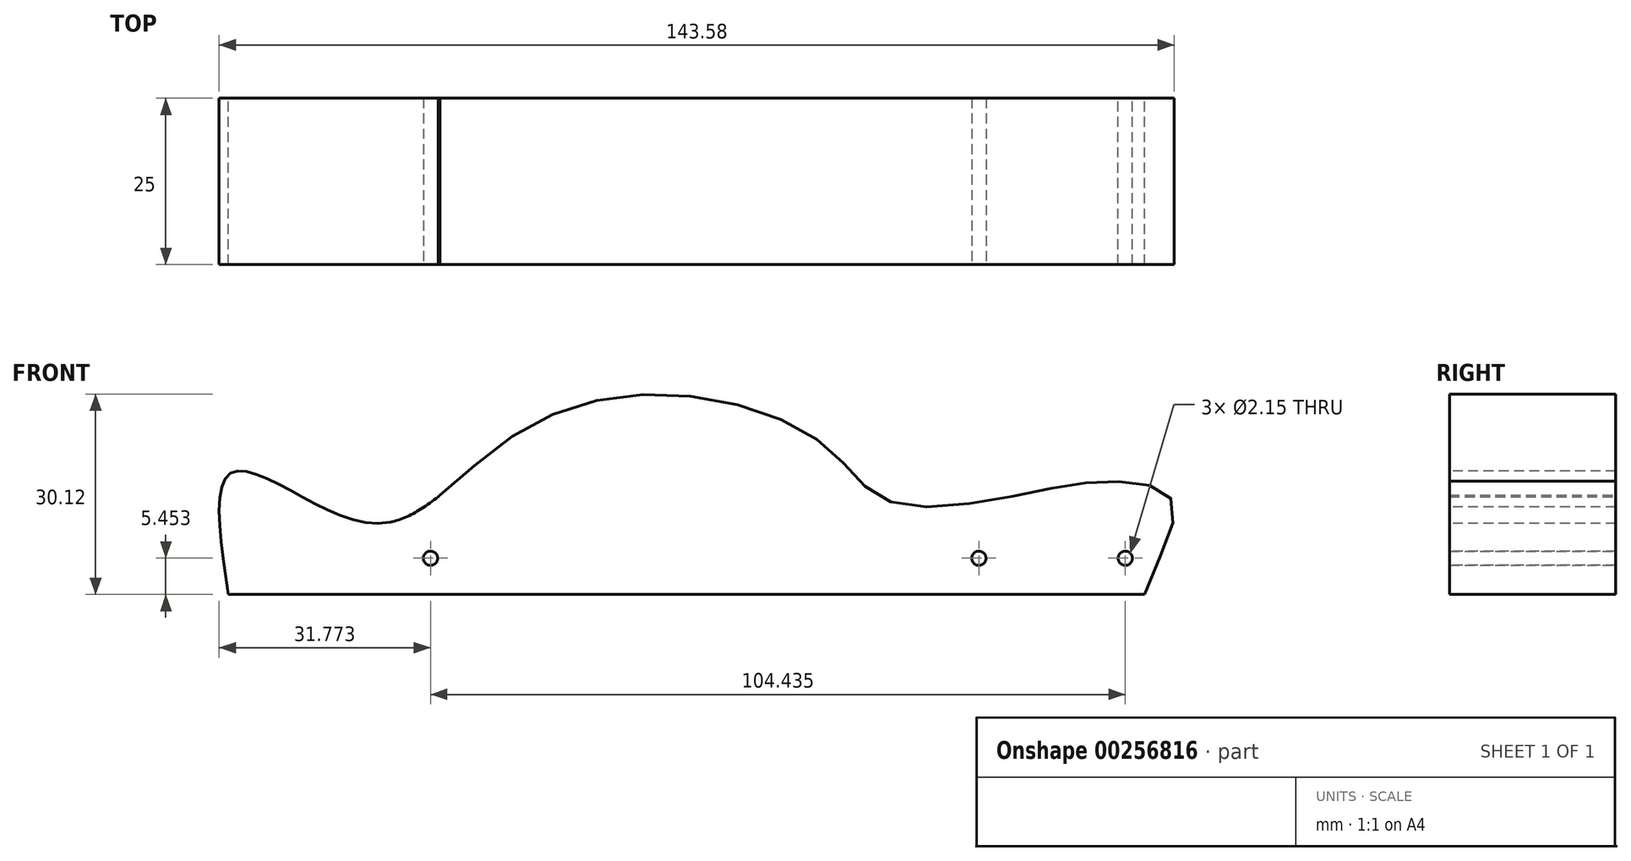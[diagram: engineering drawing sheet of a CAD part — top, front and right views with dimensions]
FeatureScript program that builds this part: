
annotation { "Feature Type Name" : "Feature", "Feature Type Description" : "" }
export const myFeature = defineFeature(function(context is Context, id is Id, definition is map)
    precondition{}
    {
        {
            var Q0;
            Q0=qCreatedBy(makeId("Front.planeOp"),FACE);
            var sketch = newSketch(context, id + "F0", { "sketchPlane" : qUnion([Q0])});
            skLineSegment(sketch, "E0", {"start": v(0, 0) * mm, "end": v(70.1, 0) * mm});
            skLineSegment(sketch, "E1", {"start": v(70.1, 0) * mm, "end": v(-67.63, 0) * mm});
            skFitSpline(sketch, "E2", {"points": [v(-67.63, 0) * mm, v(-67.63, 18) * mm, v(-58.54, 15.78) * mm, v(-43.29, 10.87) * mm, v(-24.86, 23.85) * mm, v(0, 30) * mm, v(22.28, 22.2) * mm, v(31.43, 14.07) * mm, v(51.3, 15) * mm, v(66.46, 17) * mm, v(74.34, 13.86) * mm, v(70.1, 0) * mm, v(67.74, -19.06) * mm], "startDerivative": vector(-41.87, 267.1) * mm, "endDerivative": vector(-3.35, -215.2) * mm});
            skFitSpline(sketch, "E3", {"points": [v(-35.86, 14.9) * mm, v(-36.11, 14.7) * mm, v(-43.29, 10.87) * mm], "startDerivative": vector(2.2, 1.82) * mm, "endDerivative": vector(-12.31, -7.66) * mm});
            skSolve(sketch);
        }
        {
            var Q0;
            {var subQ0=sQuery(id+"F0.wireOp",EDGE,"E2");var subQ1=sQuery(id+"F0.wireOp",EDGE,"E1");var subQ2=makeQuery(id+"F0.imprint","INTERSECT",VERTEX,{"disambiguationData":[OD(0.0)],"derivedFrom":[subQ1,subQ0]});Q0=makeQuery(id+"F0.imprint","IMPRINT",FACE,{"disambiguationData":[TD([[makeQuery(id+"F0.imprint","IMPRINT",EDGE,{"disambiguationData":[TD([[subQ2,-1.0]])],"derivedFrom":subQ1}),-1.0]])]});}
            extrude(context, id + "F1", {"entities" : qUnion([Q0]), "depth" : 25 * mm});
        }
        {
            var Q0;
            Q0=makeQuery(id+"F1.opExtrude","CAP_FACE",FACE,{"disambiguationData":[OSD([sQuery(id+"F0.wireOp",EDGE,"E1"),sQuery(id+"F0.wireOp",EDGE,"E2"),sQuery(id+"F0.wireOp",EDGE,"E3")])],"isStart":false});
            var sketch = newSketch(context, id + "F2", { "sketchPlane" : qUnion([Q0])});
            skPoint(sketch, "E4", {"position": v(45.18, 5.45) * mm});
            skPoint(sketch, "E5", {"position": v(-37.25, 5.45) * mm});
            skSolve(sketch);
        }
        {
            var Q0;
            Q0=sQuery(id+"F2.wireOp",VERTEX,"E4");
            var Q1;
            Q1=sQuery(id+"F2.wireOp",VERTEX,"E5");
            var Q2;
            Q2=makeQuery(id+"F1.opExtrude","SWEPT_BODY",BODY,{"disambiguationData":[OSD([sQuery(id+"F0.wireOp",EDGE,"E1"),sQuery(id+"F0.wireOp",EDGE,"E2"),sQuery(id+"F0.wireOp",EDGE,"E3")])]});
            hole(context, id + "F3", {"style" : HoleStyle.SIMPLE, "endStyle" : HoleEndStyle.THROUGH, "holeDiameter" : 2.15 * mm, "tappedDepth" : 12 * mm, "tapClearance" : 3, "startFromSketch" : true, "locations" : qUnion([Q0, Q1]), "scope" : qUnion([Q2])});
        }
        {
            var Q0;
            Q0=makeQuery(id+"F1.opExtrude","CAP_FACE",FACE,{"disambiguationData":[OSD([sQuery(id+"F0.wireOp",EDGE,"E1"),sQuery(id+"F0.wireOp",EDGE,"E2"),sQuery(id+"F0.wireOp",EDGE,"E3")])],"isStart":true});
            var sketch = newSketch(context, id + "F4", { "sketchPlane" : qUnion([Q0])});
            skPoint(sketch, "E6", {"position": v(-67.19, 5.45) * mm});
            skPoint(sketch, "E7.start.orphan", {"position": v(-45.18, 5.45) * mm});
            skCircle(sketch, "E8", {"center": v(-67.19, 5.45) * mm, "radius": 1.07 * mm});
            skSolve(sketch);
        }
        {
            var Q0;
            Q0=makeQuery(id+"F4.imprint","IMPRINT",FACE,{"disambiguationData":[TD([[makeQuery(id+"F4.imprint","IMPRINT",EDGE,{"derivedFrom":sQuery(id+"F4.wireOp",EDGE,"E8")}),1.0]])]});
            extrude(context, id + "F5", {"entities" : qUnion([Q0]), "operationType" : NewBodyOperationType.REMOVE, "endBound" : BoundingType.THROUGH_ALL, "oppositeDirection" : true, "depth" : 25 * mm});
        }
    });
